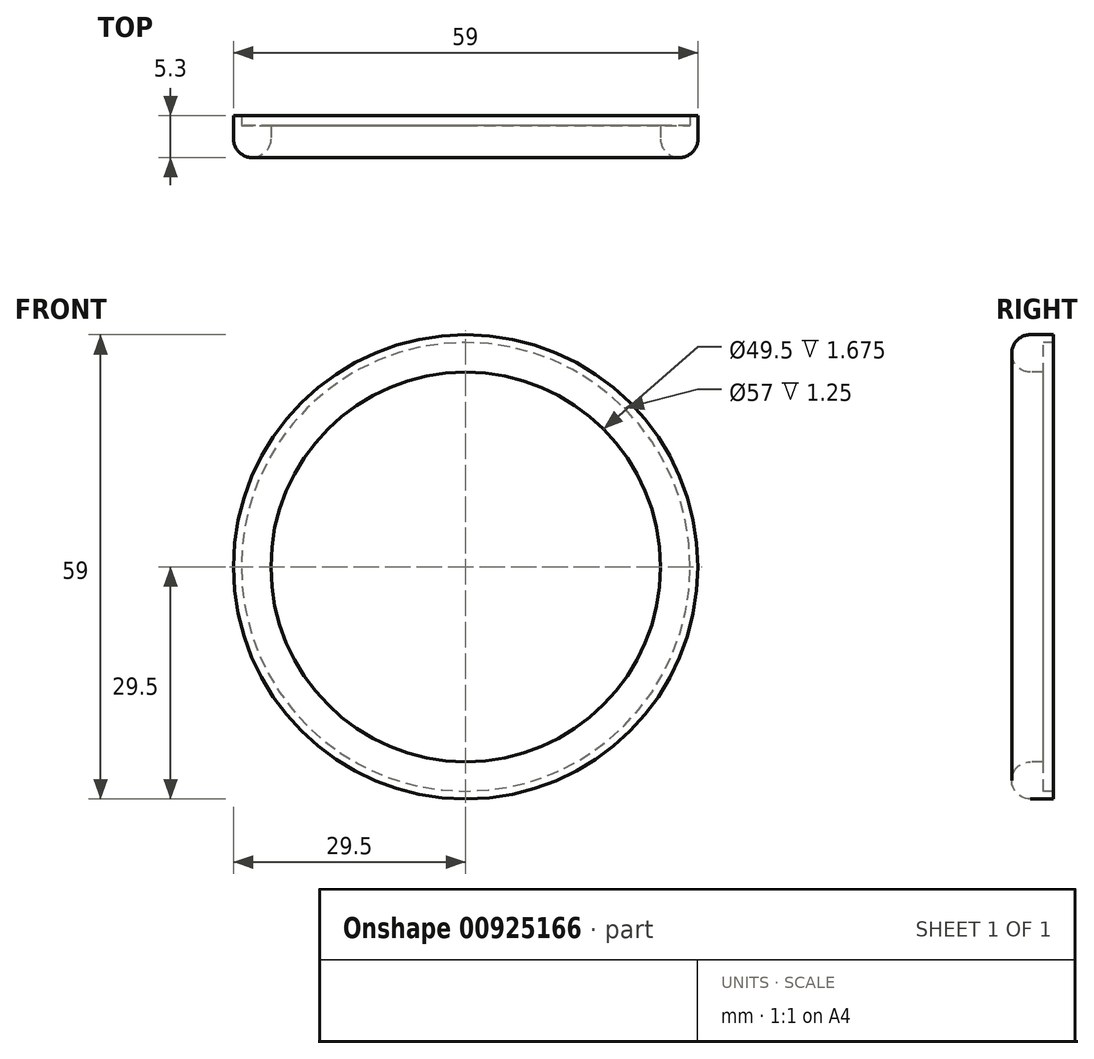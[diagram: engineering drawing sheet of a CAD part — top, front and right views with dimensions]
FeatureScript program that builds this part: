
annotation { "Feature Type Name" : "Feature", "Feature Type Description" : "" }
export const myFeature = defineFeature(function(context is Context, id is Id, definition is map)
    precondition{}
    {
        {
            var Q0;
            Q0=qCreatedBy(makeId("Right.planeOp"),FACE);
            var sketch = newSketch(context, id + "F0", { "sketchPlane" : qUnion([Q0])});
            skLineSegment(sketch, "E0", {"start": v(-23.85, 0) * mm, "end": v(29.78, 0) * mm, "construction": true});
            skLineSegment(sketch, "E1", {"start": v(0, 29.5) * mm, "end": v(-2.92, 29.5) * mm});
            skLineSegment(sketch, "E2", {"start": v(-5.3, 27.13) * mm, "end": v(-5.3, 27.12) * mm});
            skLineSegment(sketch, "E3", {"start": v(-2.92, 24.75) * mm, "end": v(-1.25, 24.75) * mm});
            skLineSegment(sketch, "E4", {"start": v(-1.25, 24.75) * mm, "end": v(-1.25, 28.5) * mm});
            skLineSegment(sketch, "E5", {"start": v(-1.25, 28.5) * mm, "end": v(0, 28.5) * mm});
            skLineSegment(sketch, "E6", {"start": v(0, 28.5) * mm, "end": v(0, 29.5) * mm});
            skPoint(sketch, "E7.visualSharp", {"position": v(-5.3, 29.5) * mm});
            skArc(sketch, "E7.filletArc", {"start": v(-2.93, 29.5) * mm, "mid": v(-4.6, 28.8) * mm, "end": v(-5.3, 27.13) * mm});
            skPoint(sketch, "E8.visualSharp", {"position": v(-5.3, 24.75) * mm});
            skArc(sketch, "E8.filletArc", {"start": v(-5.3, 27.12) * mm, "mid": v(-4.6, 25.45) * mm, "end": v(-2.92, 24.75) * mm});
            skSolve(sketch);
        }
        {
            var Q0;
            Q0 = qSketchRegion(id + "F0", true);
            var Q1;
            Q1=sQuery(id+"F0.wireOp",EDGE,"E0");
            revolve(context, id + "F1", {"surfaceOperationType" : NewSurfaceOperationType.NEW, "entities" : qUnion([Q0]), "axis" : qUnion([Q1]), "revolveType" : RevolveType.FULL});
        }
    });
